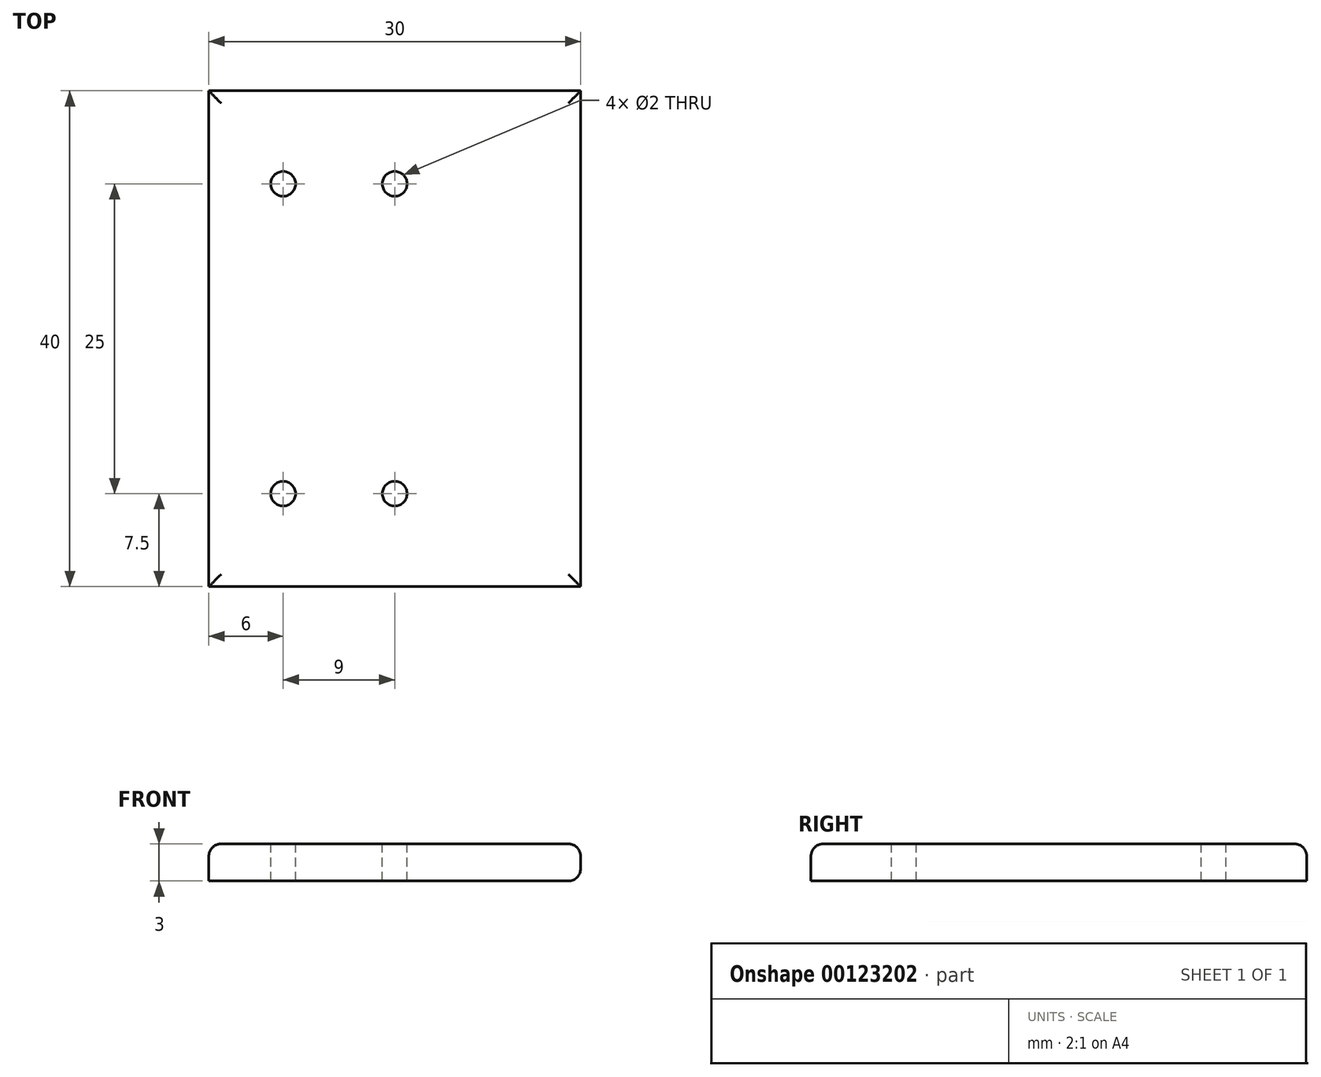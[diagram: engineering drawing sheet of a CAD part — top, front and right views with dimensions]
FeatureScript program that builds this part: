
annotation { "Feature Type Name" : "Feature", "Feature Type Description" : "" }
export const myFeature = defineFeature(function(context is Context, id is Id, definition is map)
    precondition{}
    {
        {
            var Q0;
            Q0=qCreatedBy(makeId("Top.planeOp"),FACE);
            var sketch = newSketch(context, id + "F0", { "sketchPlane" : qUnion([Q0])});
            skLineSegment(sketch, "E0.bottom", {"start": v(15, -20) * mm, "end": v(-15, -20) * mm});
            skLineSegment(sketch, "E0.top", {"start": v(15, 20) * mm, "end": v(-15, 20) * mm});
            skLineSegment(sketch, "E0.left", {"start": v(15, -20) * mm, "end": v(15, 20) * mm});
            skLineSegment(sketch, "E0.right", {"start": v(-15, -20) * mm, "end": v(-15, 20) * mm});
            skPoint(sketch, "E0.middle", {"position": v(0, 0) * mm});
            skCircle(sketch, "E1", {"center": v(-9, 12.5) * mm, "radius": 1 * mm});
            skCircle(sketch, "E2", {"center": v(0, 12.5) * mm, "radius": 1 * mm});
            skCircle(sketch, "E3", {"center": v(-9, -12.5) * mm, "radius": 1 * mm});
            skCircle(sketch, "E4", {"center": v(0, -12.5) * mm, "radius": 1 * mm});
            skSolve(sketch);
        }
        {
            var Q0;
            Q0=makeQuery(id+"F0.imprint","IMPRINT",FACE,{"disambiguationData":[TD([[makeQuery(id+"F0.imprint","IMPRINT",EDGE,{"derivedFrom":sQuery(id+"F0.wireOp",EDGE,"1teqIkxE-H5vS-1LeK-UrZz-mUXFkpOT8qA6.bottom")}),-1.0]])]});
            var Q1;
            Q1=makeQuery(id+"F0.imprint","IMPRINT",FACE,{"disambiguationData":[TD([[makeQuery(id+"F0.imprint","IMPRINT",EDGE,{"derivedFrom":sQuery(id+"F0.wireOp",EDGE,"E0.bottom")}),-1.0]])]});
            extrude(context, id + "F1", {"entities" : qUnion([Q0, Q1]), "oppositeDirection" : true, "depth" : 3 * mm});
        }
        {
            var Q0;
            Q0=makeQuery(id+"F1.opExtrude","CAP_EDGE",EDGE,{"disambiguationData":[OSD([sQuery(id+"F0.wireOp",EDGE,"E0.right")])],"isStart":true});
            var Q1;
            Q1=makeQuery(id+"F1.opExtrude","CAP_EDGE",EDGE,{"disambiguationData":[OSD([sQuery(id+"F0.wireOp",EDGE,"E0.top")])],"isStart":true});
            var Q2;
            Q2=makeQuery(id+"F1.opExtrude","CAP_EDGE",EDGE,{"disambiguationData":[OSD([sQuery(id+"F0.wireOp",EDGE,"E0.left")])],"isStart":true});
            var Q3;
            Q3=makeQuery(id+"F1.opExtrude","CAP_EDGE",EDGE,{"disambiguationData":[OSD([sQuery(id+"F0.wireOp",EDGE,"E0.bottom")])],"isStart":true});
            var Q4;
            Q4=makeQuery(id+"F1.opExtrude","CAP_EDGE",EDGE,{"disambiguationData":[OSD([sQuery(id+"F0.wireOp",EDGE,"E0.left")])],"isStart":false});
            fillet(context, id + "F2", {"entities" : qUnion([Q0, Q1, Q2, Q3, Q4]), "radius" : 1 * mm, "tangentPropagation" : true, "allowEdgeOverflow" : false});
        }
    });
